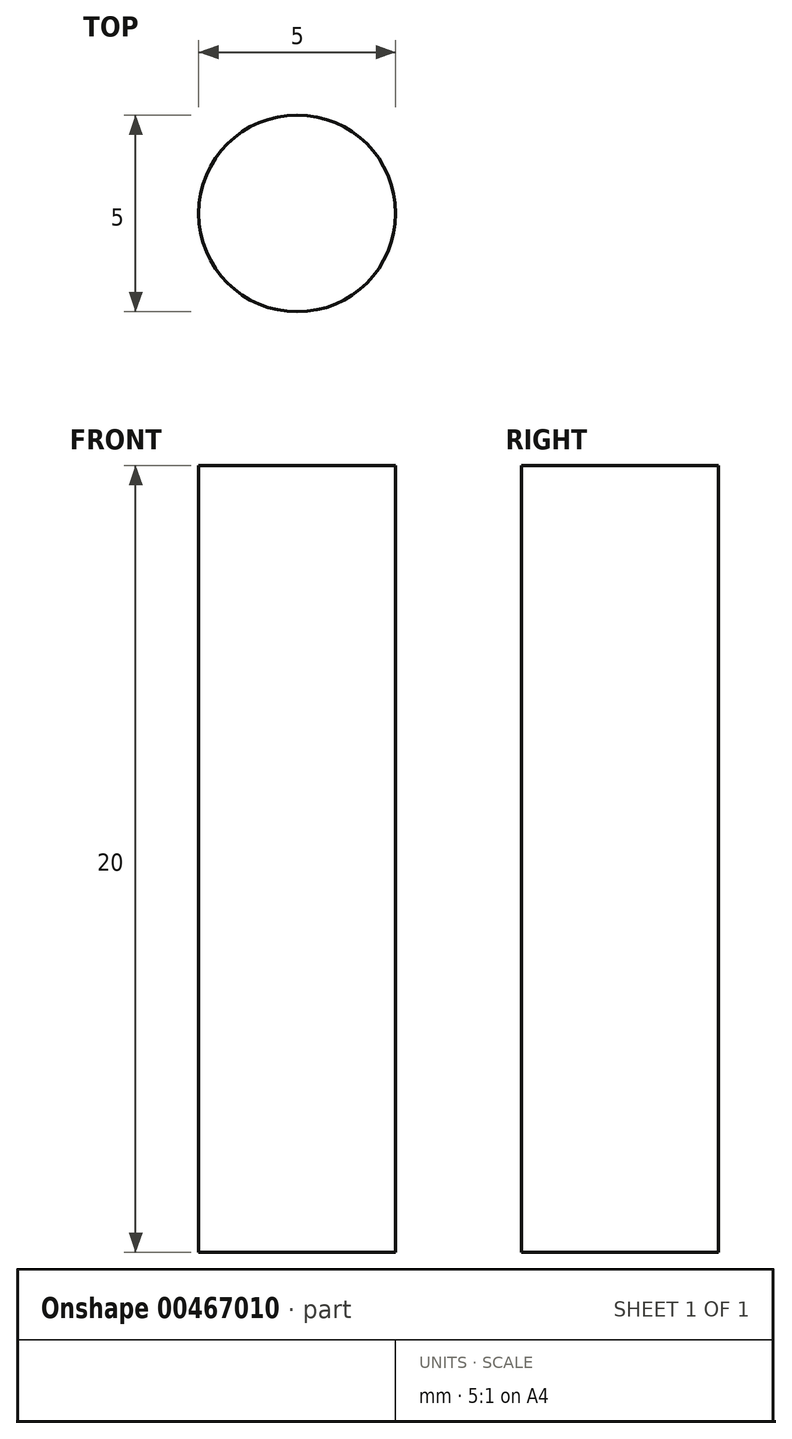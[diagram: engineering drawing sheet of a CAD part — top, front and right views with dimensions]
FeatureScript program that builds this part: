
annotation { "Feature Type Name" : "Feature", "Feature Type Description" : "" }
export const myFeature = defineFeature(function(context is Context, id is Id, definition is map)
    precondition{}
    {
        {
            var Q0;
            Q0=qCreatedBy(makeId("Top.planeOp"),FACE);
            var sketch = newSketch(context, id + "F0", { "sketchPlane" : qUnion([Q0])});
            skCircle(sketch, "E0", {"center": v(0, 0) * mm, "radius": 2.5 * mm});
            skSolve(sketch);
        }
        {
            var Q0;
            Q0 = qSketchRegion(id + "F0", true);
            extrude(context, id + "F1", {"entities" : qUnion([Q0]), "depth" : 20 * mm});
        }
    });
